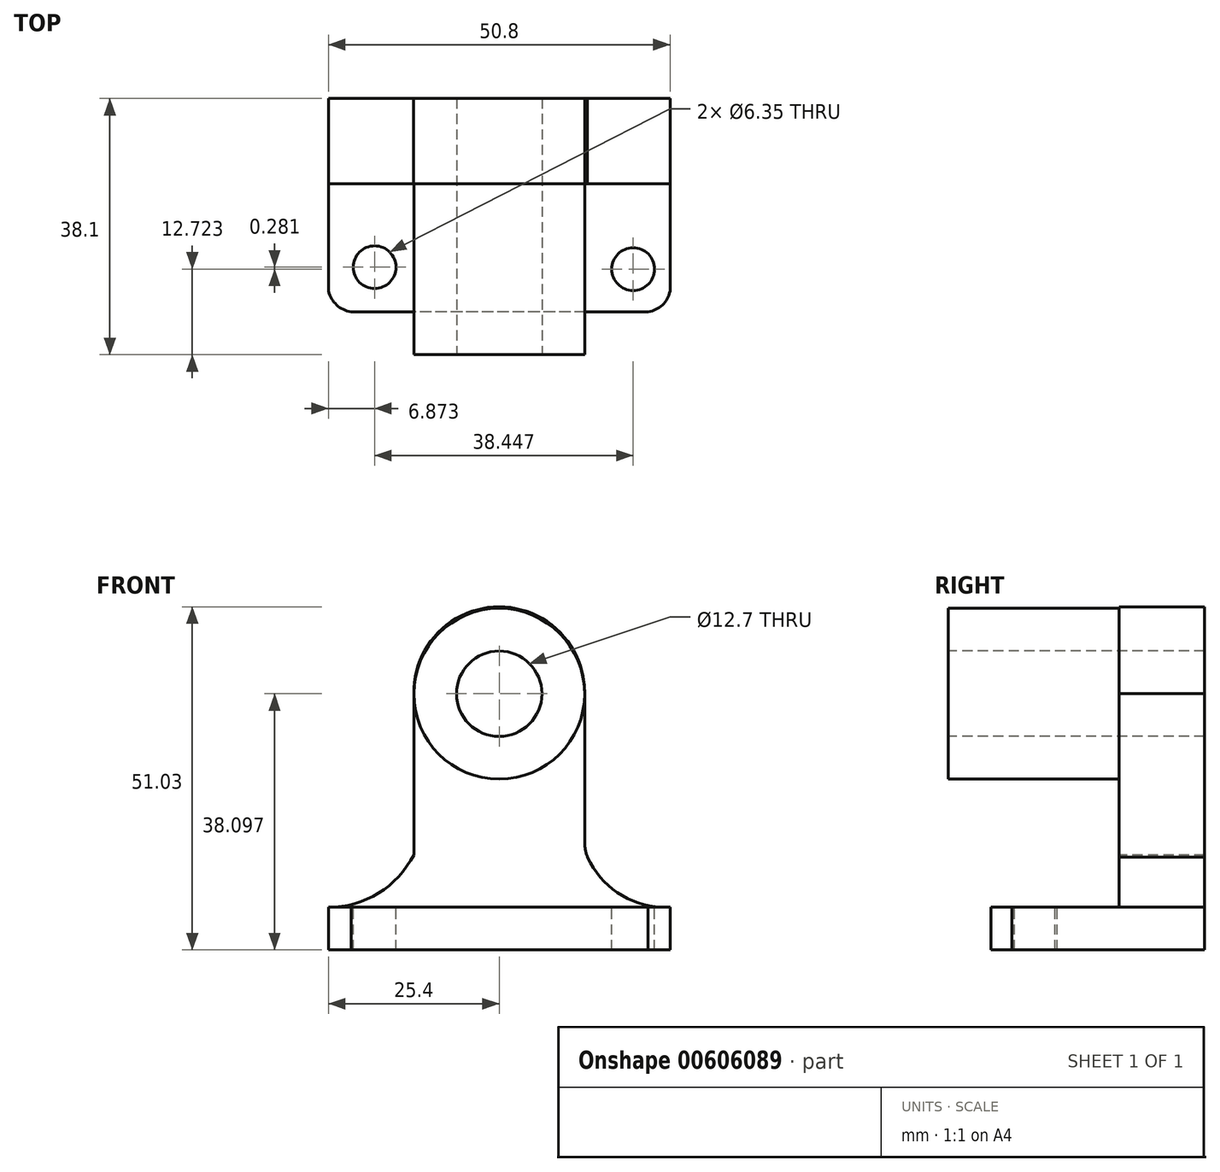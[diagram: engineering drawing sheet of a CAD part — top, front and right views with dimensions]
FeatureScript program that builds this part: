
annotation { "Feature Type Name" : "Feature", "Feature Type Description" : "" }
export const myFeature = defineFeature(function(context is Context, id is Id, definition is map)
    precondition{}
    {
        {
            var Q0;
            Q0=qCreatedBy(makeId("Right.planeOp"),FACE);
            var sketch = newSketch(context, id + "F0", { "sketchPlane" : qUnion([Q0])});
            skLineSegment(sketch, "E0", {"start": v(58.15, 55.07) * mm, "end": v(58.15, 16.97) * mm});
            skLineSegment(sketch, "E1", {"start": v(58.15, 16.97) * mm, "end": v(26.4, 16.97) * mm});
            skLineSegment(sketch, "E2", {"start": v(26.4, 16.97) * mm, "end": v(26.4, 23.32) * mm});
            skLineSegment(sketch, "E3", {"start": v(26.4, 23.32) * mm, "end": v(45.45, 23.32) * mm});
            skLineSegment(sketch, "E4", {"start": v(45.45, 23.32) * mm, "end": v(45.45, 55.07) * mm});
            skLineSegment(sketch, "E5", {"start": v(45.45, 55.07) * mm, "end": v(58.15, 55.07) * mm});
            skSolve(sketch);
        }
        {
            var Q0;
            Q0 = qSketchRegion(id + "F0", true);
            extrude(context, id + "F1", {"entities" : qUnion([Q0]), "depth" : 50.8 * mm, "offsetDistance" : 25.4 * mm});
        }
        {
            var Q0;
            Q0=makeQuery(id+"F1.opExtrude","SWEPT_FACE",FACE,{"disambiguationData":[OSD([sQuery(id+"F0.wireOp",EDGE,"E4")])]});
            var sketch = newSketch(context, id + "F2", { "sketchPlane" : qUnion([Q0])});
            skLineSegment(sketch, "E6", {"start": v(38.1, 55.07) * mm, "end": v(38.1, 33.07) * mm});
            skLineSegment(sketch, "E7", {"start": v(38.1, 55.07) * mm, "end": v(50.8, 55.07) * mm});
            skLineSegment(sketch, "E8", {"start": v(50.8, 55.07) * mm, "end": v(50.8, 23.32) * mm});
            skPoint(sketch, "E9.visualSharp", {"position": v(38.1, 32.06) * mm});
            skArc(sketch, "E9.filletArc", {"start": v(38.1, 33.07) * mm, "mid": v(38.21, 31.89) * mm, "end": v(38.54, 30.75) * mm});
            skArc(sketch, "E10", {"start": v(38.54, 30.75) * mm, "mid": v(43.53, 25.15) * mm, "end": v(50.8, 23.32) * mm});
            skSolve(sketch);
        }
        {
            var Q0;
            Q0 = qSketchRegion(id + "F2", true);
            extrude(context, id + "F3", {"entities" : qUnion([Q0]), "operationType" : NewBodyOperationType.REMOVE, "oppositeDirection" : true, "depth" : 25.4 * mm, "offsetDistance" : 25.4 * mm});
        }
        {
            var Q0;
            Q0=makeQuery(id+"F1.opExtrude","SWEPT_FACE",FACE,{"disambiguationData":[OSD([sQuery(id+"F0.wireOp",EDGE,"E4")])]});
            var sketch = newSketch(context, id + "F4", { "sketchPlane" : qUnion([Q0])});
            skLineSegment(sketch, "E11", {"start": v(12.7, 55.07) * mm, "end": v(12.7, 31.12) * mm});
            skArc(sketch, "E12", {"start": v(0, 23.32) * mm, "mid": v(7.45, 25.42) * mm, "end": v(12.7, 31.12) * mm});
            skLineSegment(sketch, "E13", {"start": v(0, 23.32) * mm, "end": v(0, 55.07) * mm});
            skLineSegment(sketch, "E14", {"start": v(0, 55.07) * mm, "end": v(12.7, 55.07) * mm});
            skSolve(sketch);
        }
        {
            var Q0;
            Q0=makeQuery(id+"F4.imprint","IMPRINT",FACE,{"disambiguationData":[TD([[makeQuery(id+"F4.imprint","IMPRINT",EDGE,{"derivedFrom":sQuery(id+"F4.wireOp",EDGE,"E11")}),-1.0]])]});
            extrude(context, id + "F5", {"entities" : qUnion([Q0]), "operationType" : NewBodyOperationType.REMOVE, "oppositeDirection" : true, "depth" : 25.4 * mm, "offsetDistance" : 25.4 * mm});
        }
        {
            var Q0;
            Q0=makeQuery(id+"F1.opExtrude","SWEPT_FACE",FACE,{"disambiguationData":[OSD([sQuery(id+"F0.wireOp",EDGE,"E4")])]});
            var sketch = newSketch(context, id + "F6", { "sketchPlane" : qUnion([Q0])});
            skCircle(sketch, "E15", {"center": v(25.4, 55.07) * mm, "radius": 12.7 * mm});
            skSolve(sketch);
        }
        {
            var Q0;
            Q0 = qSketchRegion(id + "F6", true);
            extrude(context, id + "F7", {"entities" : qUnion([Q0]), "operationType" : NewBodyOperationType.ADD, "depth" : 25.4 * mm, "offsetDistance" : 25.4 * mm});
        }
        {
            var Q0;
            Q0=makeQuery(id+"F7.opExtrude","CAP_FACE",FACE,{"disambiguationData":[OSD([sQuery(id+"F6.wireOp",EDGE,"E15")])],"isStart":true});
            var sketch = newSketch(context, id + "F8", { "sketchPlane" : qUnion([Q0])});
            skArc(sketch, "E16", {"start": v(-12.7, 55.07) * mm, "mid": v(-25.4, 68) * mm, "end": v(-38.1, 55.07) * mm});
            skLineSegment(sketch, "E17", {"start": v(-38.1, 55.07) * mm, "end": v(-12.7, 55.07) * mm});
            skSolve(sketch);
        }
        {
            var Q0;
            Q0 = qSketchRegion(id + "F8", true);
            extrude(context, id + "F9", {"entities" : qUnion([Q0]), "operationType" : NewBodyOperationType.ADD, "depth" : 12.7 * mm, "offsetDistance" : 25.4 * mm});
        }
        {
            var Q0;
            Q0=makeQuery(id+"F7.opExtrude","CAP_FACE",FACE,{"disambiguationData":[OSD([sQuery(id+"F6.wireOp",EDGE,"E15")])],"isStart":false});
            var sketch = newSketch(context, id + "F10", { "sketchPlane" : qUnion([Q0])});
            skCircle(sketch, "E18", {"center": v(25.4, 55.07) * mm, "radius": 6.35 * mm});
            skSolve(sketch);
        }
        {
            var Q0;
            Q0 = qSketchRegion(id + "F10", true);
            extrude(context, id + "F11", {"entities" : qUnion([Q0]), "operationType" : NewBodyOperationType.REMOVE, "oppositeDirection" : true, "depth" : 38.1 * mm, "offsetDistance" : 25.4 * mm});
        }
        {
            var Q0;
            Q0=makeQuery(id+"F1.opExtrude","SWEPT_FACE",FACE,{"disambiguationData":[OSD([sQuery(id+"F0.wireOp",EDGE,"E3")])]});
            var sketch = newSketch(context, id + "F12", { "sketchPlane" : qUnion([Q0])});
            skArc(sketch, "E19", {"start": v(0, 31.54) * mm, "mid": v(0.97, 27.7) * mm, "end": v(4.7, 26.4) * mm});
            skLineSegment(sketch, "E20", {"start": v(0, 31.54) * mm, "end": v(0, 26.4) * mm});
            skLineSegment(sketch, "E21", {"start": v(0, 26.4) * mm, "end": v(4.7, 26.4) * mm});
            skSolve(sketch);
        }
        {
            var Q0;
            Q0 = qSketchRegion(id + "F12", true);
            extrude(context, id + "F13", {"entities" : qUnion([Q0]), "operationType" : NewBodyOperationType.REMOVE, "oppositeDirection" : true, "depth" : 6.35 * mm, "offsetDistance" : 25.4 * mm});
        }
        {
            var Q0;
            Q0=makeQuery(id+"F1.opExtrude","SWEPT_FACE",FACE,{"disambiguationData":[OSD([sQuery(id+"F0.wireOp",EDGE,"E3")])]});
            var sketch = newSketch(context, id + "F14", { "sketchPlane" : qUnion([Q0])});
            skArc(sketch, "E22", {"start": v(46.42, 26.4) * mm, "mid": v(49.23, 27.08) * mm, "end": v(50.8, 29.5) * mm});
            skLineSegment(sketch, "E23", {"start": v(46.42, 26.4) * mm, "end": v(50.8, 26.4) * mm});
            skLineSegment(sketch, "E24", {"start": v(50.8, 26.4) * mm, "end": v(50.8, 29.5) * mm});
            skSolve(sketch);
        }
        {
            var Q0;
            Q0 = qSketchRegion(id + "F14", true);
            extrude(context, id + "F15", {"entities" : qUnion([Q0]), "operationType" : NewBodyOperationType.REMOVE, "oppositeDirection" : true, "depth" : 6.35 * mm, "offsetDistance" : 25.4 * mm});
        }
        {
            var Q0;
            Q0=makeQuery(id+"F1.opExtrude","SWEPT_FACE",FACE,{"disambiguationData":[OSD([sQuery(id+"F0.wireOp",EDGE,"E3")])]});
            var sketch = newSketch(context, id + "F16", { "sketchPlane" : qUnion([Q0])});
            skCircle(sketch, "E25", {"center": v(6.87, 33.05) * mm, "radius": 3.18 * mm});
            skCircle(sketch, "E26", {"center": v(45.32, 32.77) * mm, "radius": 3.18 * mm});
            skSolve(sketch);
        }
        {
            var Q0;
            Q0 = qSketchRegion(id + "F16", true);
            extrude(context, id + "F17", {"entities" : qUnion([Q0]), "operationType" : NewBodyOperationType.REMOVE, "oppositeDirection" : true, "depth" : 6.35 * mm, "offsetDistance" : 25.4 * mm});
        }
    });
